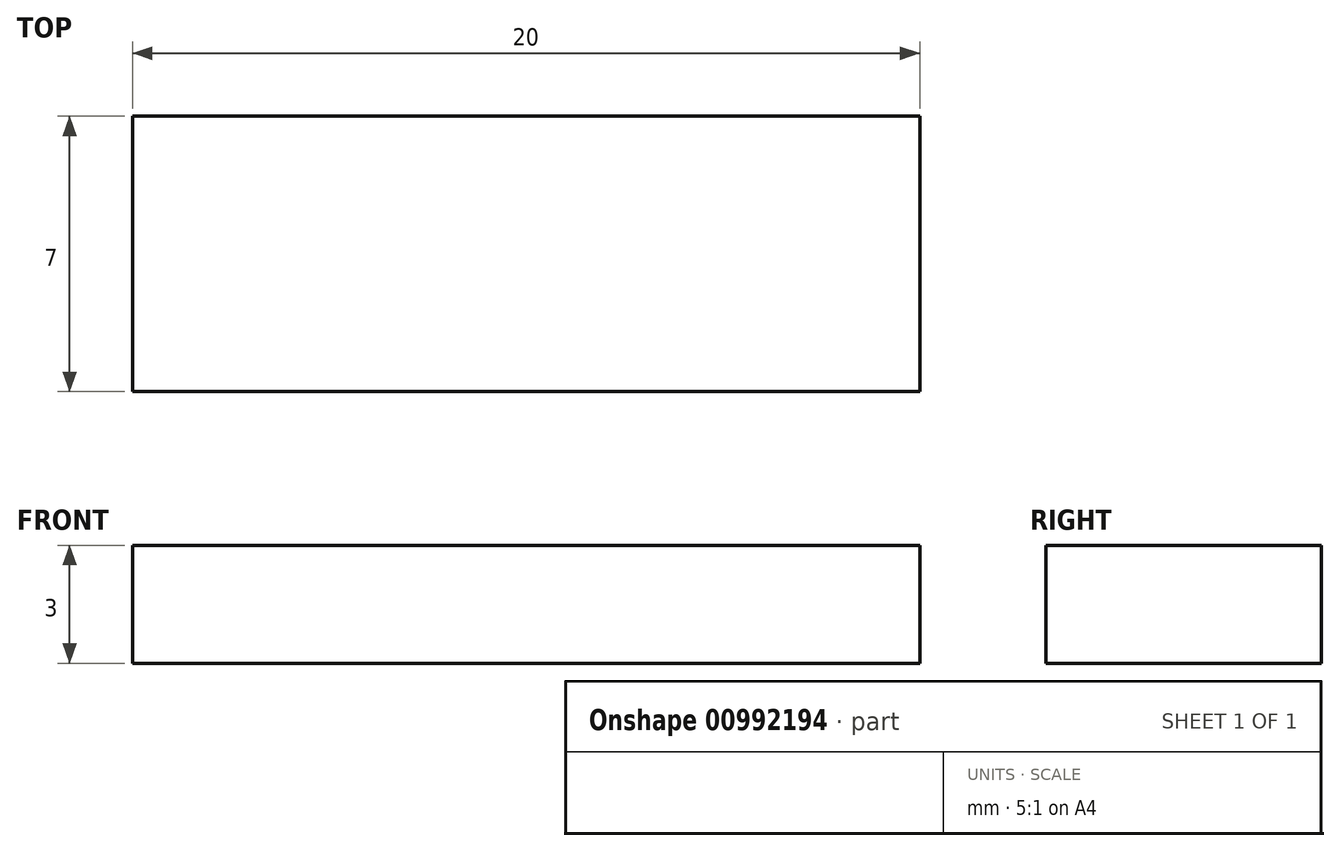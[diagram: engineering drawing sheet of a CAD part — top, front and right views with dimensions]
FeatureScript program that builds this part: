
annotation { "Feature Type Name" : "Feature", "Feature Type Description" : "" }
export const myFeature = defineFeature(function(context is Context, id is Id, definition is map)
    precondition{}
    {
        {
            var Q0;
            Q0=qCreatedBy(makeId("Top.planeOp"),FACE);
            var sketch = newSketch(context, id + "F0", { "sketchPlane" : qUnion([Q0])});
            skLineSegment(sketch, "E0.bottom", {"start": v(-10, 3.5) * mm, "end": v(10, 3.5) * mm});
            skLineSegment(sketch, "E0.top", {"start": v(-10, -3.5) * mm, "end": v(10, -3.5) * mm});
            skLineSegment(sketch, "E0.left", {"start": v(-10, 3.5) * mm, "end": v(-10, -3.5) * mm});
            skLineSegment(sketch, "E0.right", {"start": v(10, 3.5) * mm, "end": v(10, -3.5) * mm});
            skPoint(sketch, "E0.middle", {"position": v(0, 0) * mm});
            skSolve(sketch);
        }
        {
            var Q0;
            Q0 = qSketchRegion(id + "F0", true);
            extrude(context, id + "F1", {"entities" : qUnion([Q0]), "depth" : 3 * mm, "offsetDistance" : 25 * mm});
        }
    });
